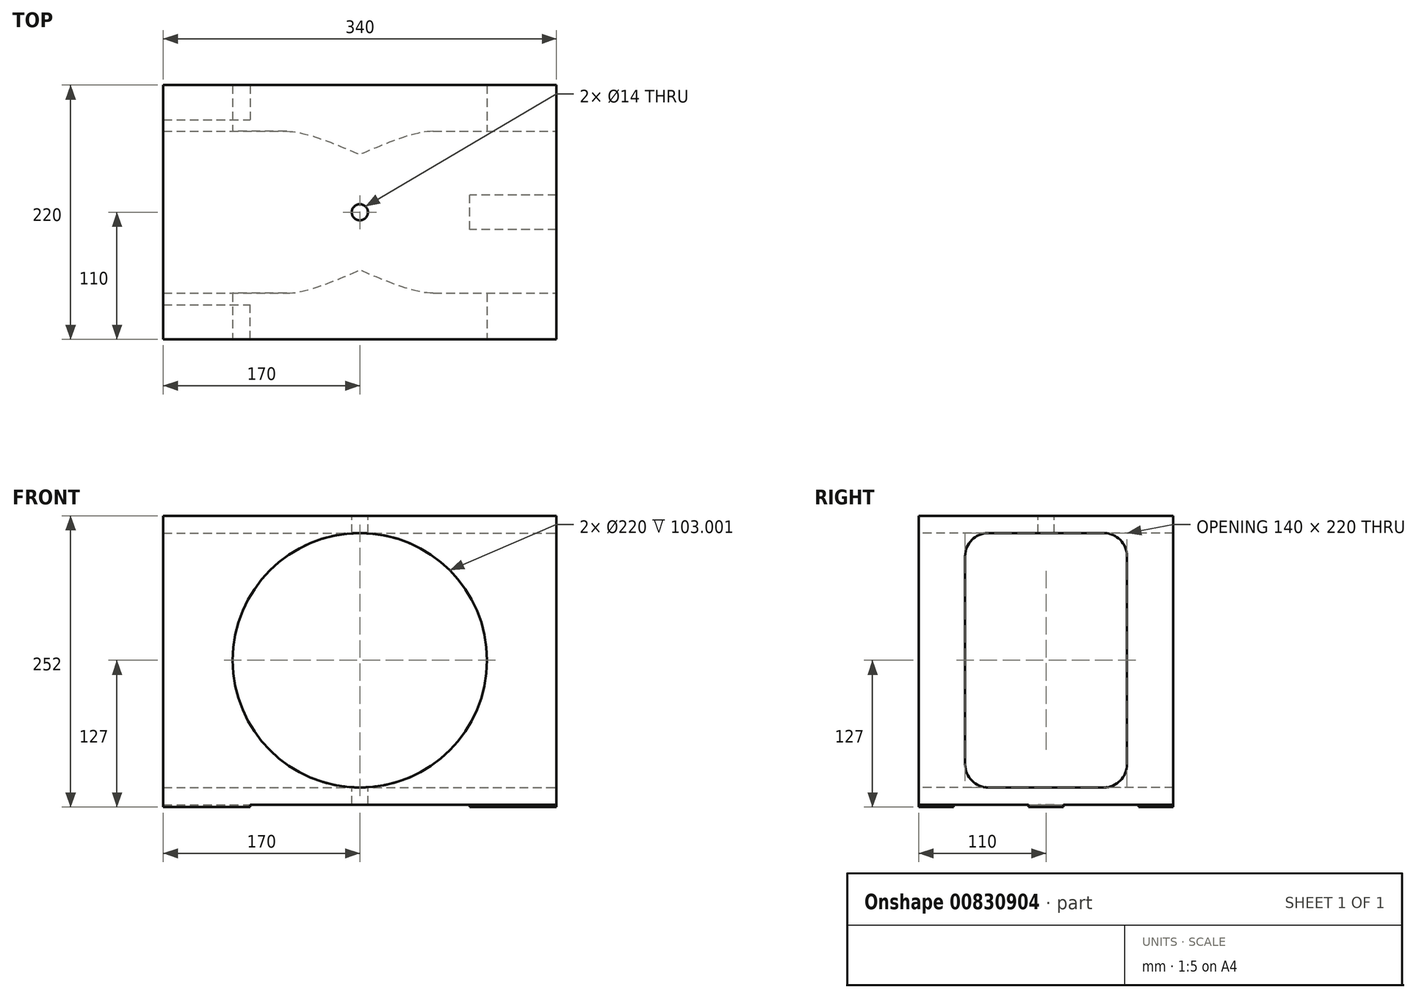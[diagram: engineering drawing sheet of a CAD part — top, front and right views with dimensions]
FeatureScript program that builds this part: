
annotation { "Feature Type Name" : "Feature", "Feature Type Description" : "" }
export const myFeature = defineFeature(function(context is Context, id is Id, definition is map)
    precondition{}
    {
        {
            var Q0;
            Q0=qCreatedBy(makeId("Front.planeOp"),FACE);
            var sketch = newSketch(context, id + "F0", { "sketchPlane" : qUnion([Q0])});
            skLineSegment(sketch, "E0.bottom", {"start": v(170, 125) * mm, "end": v(-170, 125) * mm});
            skLineSegment(sketch, "E0.top", {"start": v(170, -125) * mm, "end": v(-170, -125) * mm});
            skLineSegment(sketch, "E0.left", {"start": v(170, 125) * mm, "end": v(170, -125) * mm});
            skLineSegment(sketch, "E0.right", {"start": v(-170, 125) * mm, "end": v(-170, -125) * mm});
            skPoint(sketch, "E0.middle", {"position": v(0, 0) * mm});
            skSolve(sketch);
        }
        {
            var Q0;
            Q0 = qSketchRegion(id + "F0", true);
            extrude(context, id + "F1", {"entities" : qUnion([Q0]), "depth" : 220 * mm, "offsetDistance" : 25.4 * mm});
        }
        {
            var Q0;
            Q0=makeQuery(id+"F1.opExtrude","SWEPT_FACE",FACE,{"disambiguationData":[OSD([sQuery(id+"F0.wireOp",EDGE,"E0.left")])]});
            var sketch = newSketch(context, id + "F2", { "sketchPlane" : qUnion([Q0])});
            skLineSegment(sketch, "E1.bottom", {"start": v(-60.01, 110) * mm, "end": v(-159.99, 110) * mm});
            skLineSegment(sketch, "E1.top", {"start": v(-60.01, -110) * mm, "end": v(-159.99, -110) * mm});
            skLineSegment(sketch, "E1.left", {"start": v(-40, 89.99) * mm, "end": v(-40, -89.99) * mm});
            skLineSegment(sketch, "E1.right", {"start": v(-180, 89.99) * mm, "end": v(-180, -89.99) * mm});
            skPoint(sketch, "E1.middle", {"position": v(-110, 0) * mm});
            skPoint(sketch, "E2.visualSharp", {"position": v(-180, 110) * mm});
            skArc(sketch, "E2.filletArc", {"start": v(-159.99, 110) * mm, "mid": v(-174.14, 104.14) * mm, "end": v(-180, 89.99) * mm});
            skPoint(sketch, "E3.visualSharp", {"position": v(-40, 110) * mm});
            skArc(sketch, "E3.filletArc", {"start": v(-40, 89.99) * mm, "mid": v(-45.86, 104.14) * mm, "end": v(-60.01, 110) * mm});
            skPoint(sketch, "E4.visualSharp", {"position": v(-40, -110) * mm});
            skArc(sketch, "E4.filletArc", {"start": v(-60.01, -110) * mm, "mid": v(-45.86, -104.14) * mm, "end": v(-40, -89.99) * mm});
            skPoint(sketch, "E5.visualSharp", {"position": v(-180, -110) * mm});
            skArc(sketch, "E5.filletArc", {"start": v(-180, -89.99) * mm, "mid": v(-174.14, -104.14) * mm, "end": v(-159.99, -110) * mm});
            skSolve(sketch);
        }
        {
            var Q0;
            Q0 = qSketchRegion(id + "F2", true);
            extrude(context, id + "F3", {"entities" : qUnion([Q0]), "operationType" : NewBodyOperationType.REMOVE, "oppositeDirection" : true, "depth" : 340 * mm, "offsetDistance" : 25.4 * mm});
        }
        {
            var Q0;
            Q0=makeQuery(id+"F1.opExtrude","CAP_FACE",FACE,{"disambiguationData":[OSD([sQuery(id+"F0.wireOp",EDGE,"E0.bottom"),sQuery(id+"F0.wireOp",EDGE,"E0.top"),sQuery(id+"F0.wireOp",EDGE,"E0.left"),sQuery(id+"F0.wireOp",EDGE,"E0.right")])],"isStart":false});
            var sketch = newSketch(context, id + "F4", { "sketchPlane" : qUnion([Q0])});
            skCircle(sketch, "E6", {"center": v(0, 0) * mm, "radius": 110 * mm});
            skSolve(sketch);
        }
        {
            var Q0;
            Q0 = qSketchRegion(id + "F4", true);
            extrude(context, id + "F5", {"entities" : qUnion([Q0]), "operationType" : NewBodyOperationType.REMOVE, "oppositeDirection" : true, "depth" : 228.6 * mm, "offsetDistance" : 25.4 * mm});
        }
        {
            var Q0;
            Q0=makeQuery(id+"F1.opExtrude","SWEPT_FACE",FACE,{"disambiguationData":[OSD([sQuery(id+"F0.wireOp",EDGE,"E0.bottom")])]});
            var sketch = newSketch(context, id + "F6", { "sketchPlane" : qUnion([Q0])});
            skCircle(sketch, "E7", {"center": v(0, -110) * mm, "radius": 7 * mm});
            skSolve(sketch);
        }
        {
            var Q0;
            Q0 = qSketchRegion(id + "F6", true);
            extrude(context, id + "F7", {"entities" : qUnion([Q0]), "operationType" : NewBodyOperationType.REMOVE, "oppositeDirection" : true, "depth" : 304.8 * mm, "offsetDistance" : 25.4 * mm});
        }
        {
            var Q0;
            Q0=makeQuery(id+"F1.opExtrude","SWEPT_FACE",FACE,{"disambiguationData":[OSD([sQuery(id+"F0.wireOp",EDGE,"E0.top")])]});
            var sketch = newSketch(context, id + "F8", { "sketchPlane" : qUnion([Q0])});
            skLineSegment(sketch, "E8.bottom", {"start": v(-170, 220) * mm, "end": v(-94.88, 220) * mm});
            skLineSegment(sketch, "E8.top", {"start": v(-170, 190) * mm, "end": v(-94.88, 190) * mm});
            skLineSegment(sketch, "E8.left", {"start": v(-170, 220) * mm, "end": v(-170, 190) * mm});
            skLineSegment(sketch, "E8.right", {"start": v(-94.88, 220) * mm, "end": v(-94.88, 190) * mm});
            skLineSegment(sketch, "E9.bottom", {"start": v(-170, 0) * mm, "end": v(-94.88, 0) * mm});
            skLineSegment(sketch, "E9.top", {"start": v(-170, 30) * mm, "end": v(-94.88, 30) * mm});
            skLineSegment(sketch, "E9.left", {"start": v(-170, 0) * mm, "end": v(-170, 30) * mm});
            skLineSegment(sketch, "E9.right", {"start": v(-94.88, 0) * mm, "end": v(-94.88, 30) * mm});
            skSolve(sketch);
        }
        {
            var Q0;
            Q0 = qSketchRegion(id + "F8", true);
            extrude(context, id + "F9", {"entities" : qUnion([Q0]), "operationType" : NewBodyOperationType.ADD, "depth" : 2 * mm, "offsetDistance" : 25.4 * mm});
        }
        {
            var Q0;
            Q0=makeQuery(id+"F1.opExtrude","SWEPT_FACE",FACE,{"disambiguationData":[OSD([sQuery(id+"F0.wireOp",EDGE,"E0.top")])]});
            var sketch = newSketch(context, id + "F10", { "sketchPlane" : qUnion([Q0])});
            skLineSegment(sketch, "E10.bottom", {"start": v(170, 125) * mm, "end": v(95, 125) * mm});
            skLineSegment(sketch, "E10.top", {"start": v(170, 95) * mm, "end": v(95, 95) * mm});
            skLineSegment(sketch, "E10.left", {"start": v(170, 125) * mm, "end": v(170, 95) * mm});
            skLineSegment(sketch, "E10.right", {"start": v(95, 125) * mm, "end": v(95, 95) * mm});
            skSolve(sketch);
        }
        {
            var Q0;
            Q0 = qSketchRegion(id + "F10", true);
            extrude(context, id + "F11", {"entities" : qUnion([Q0]), "operationType" : NewBodyOperationType.ADD, "depth" : 2 * mm, "offsetDistance" : 25.4 * mm});
        }
    });
